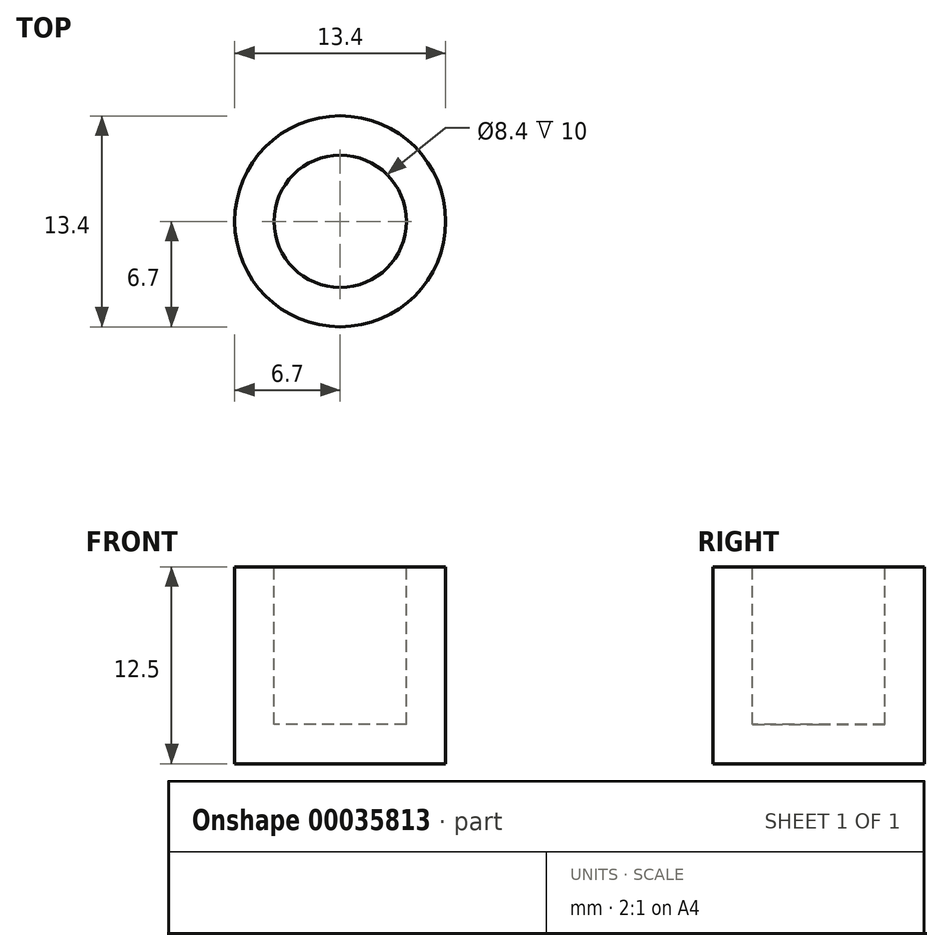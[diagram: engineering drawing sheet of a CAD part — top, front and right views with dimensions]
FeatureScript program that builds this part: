
annotation { "Feature Type Name" : "Feature", "Feature Type Description" : "" }
export const myFeature = defineFeature(function(context is Context, id is Id, definition is map)
    precondition{}
    {
        {
            var Q0;
            Q0=qCreatedBy(makeId("Right.planeOp"),FACE);
            var sketch = newSketch(context, id + "F0", { "sketchPlane" : qUnion([Q0])});
            skLineSegment(sketch, "E0", {"start": v(0, 0) * mm, "end": v(0, 2.5) * mm});
            skLineSegment(sketch, "E1", {"start": v(0, 2.5) * mm, "end": v(-4.2, 2.5) * mm});
            skLineSegment(sketch, "E2", {"start": v(-4.2, 2.5) * mm, "end": v(-4.2, 12.5) * mm});
            skLineSegment(sketch, "E3", {"start": v(-4.2, 12.5) * mm, "end": v(-6.7, 12.5) * mm});
            skLineSegment(sketch, "E4", {"start": v(-6.7, 12.5) * mm, "end": v(-6.7, 0) * mm});
            skLineSegment(sketch, "E5", {"start": v(-6.7, 0) * mm, "end": v(0, 0) * mm});
            skLineSegment(sketch, "E6", {"start": v(0, 73) * mm, "end": v(0, -36.27) * mm, "construction": true});
            skSolve(sketch);
        }
        {
            var Q0;
            Q0=makeQuery(id+"F0.imprint","IMPRINT",FACE,{"disambiguationData":[TD([[makeQuery(id+"F0.imprint","IMPRINT",EDGE,{"derivedFrom":sQuery(id+"F0.wireOp",EDGE,"E0")}),1.0]])]});
            var Q1;
            Q1=sQuery(id+"F0.wireOp",EDGE,"E6");
            revolve(context, id + "F1", {"entities" : qUnion([Q0]), "axis" : qUnion([Q1]), "revolveType" : RevolveType.FULL});
        }
    });
